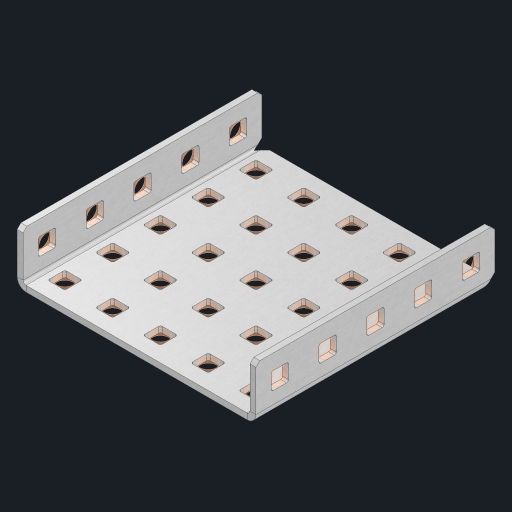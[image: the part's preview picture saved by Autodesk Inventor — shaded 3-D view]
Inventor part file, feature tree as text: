
AUTODESK INVENTOR PART (.ipt)
format: ipt  version: 2023 (Build 270158000, 158)  size: 696,320 bytes
history: native  units: in
note: dims shown in document units (in); Inventor stores cm internally (conversion verified against a paired STEP export)
features: other x40, extrude x34, sheet_metal_op x10, sketch x8, mirror x1, pattern_linear x1, chamfer x1
ambient origin geometry x8: Origin, YZ Plane, XZ Plane, XY Plane, X Axis, Y Axis, Z Axis, Center Point
bodies: Solid1 (feature_tree), Body (feature_tree)
feature tree (95):
  other  "Flange Pattern Plane"
  sheet_metal_op  "Flange Pattern"
  sheet_metal_op  "Body Pattern"
  other  "Arc Length"
  mirror  "Notch Mirror"
  pattern_linear  "Notch Pattern"  Spacing1=0.25in  [1 undecoded]
  chamfer  "End Chamfer"
  extrude  "Half Cut"  Depth=0.0625in
  sketch  "Sketch1"  dims[d0=2.5in]
  other  "Plate1"
  sketch  "Sketch2"  dims[d1=2.5in]
  other  "Plate2"
  sheet_metal_op  "Bend1"
  sheet_metal_op  "Corner1"
  sketch  "Sketch3"  dims[d2=0.0625in]
  other  "Flange Pattern Sketch"
  sketch  "Sketch7"  dims[d3=0.0625in]
  other  "Srf1"
  other  "Srf2"
  sketch  "Sketch8"  dims[d4=0.0312in]
  sketch  "Sketch9"  dims[d5=0.125in]
  other  "Srf91"
  sheet_metal_op  "Body Pattern Sketch"
  other  "Srf92"
  sketch  "Sketch13"  dims[d6=0.0625in]
  sketch  "Sketch14"  dims[d7=0.5in d8=90.0deg d9=0.0312in d10=0.25in d11=0.0625in d12=0.0625in d16=0.182in d17=0.02in d18=0.0625in d19=0.0in d20=0.25in d21=0.25in d46=0.172in d47=1.0in d48=0.0in d49=0.182in d50=0.02in d51=0.25in d52=0.25in d53=0.0625in d54=0.0in d55=0.172in d56=1.0in d57=0.0in d60=1.9685in d62=0.5in d63=1.9685in d65=0.5in d85=0.1473in d86=0.1782in d88=0.04in d89=0.0625in d90=0.0in d91=0.04in d92=0.0491in d95=2.5in d96=0.04in d97=0.25in d98=45.0deg d101=0.0in d102=2.497in d131=2.5in d132=1.9685in d134=0.5in d139=0.5in]
  other  "Srf856"
  other  "Srf1310"
  other  "Srf1311"
  other  "Srf1312"
  other  "Srf1376"
  other  "Srf1377"
  other  "Srf1728"
  other  "Srf1755"
  other  "Srf1878"
  other  "Srf1879"
  other  "Srf1880"
  other  "Srf1881"
  other  "Srf1942"
  other  "Srf1943"
  other  "Srf1944"
  other  "Srf1945"
  other  "Srf1946"
  other  "Srf1947"
  other  "Srf1948"
  other  "Srf1949"
  other  "Srf1950"
  other  "Srf1951"
  other  "Srf1952"
  other  "Srf1953"
  other  "Srf1954"
  other  "Srf1955"
  other  "Srf1956"
  other  "Srf1957"
  other  "Srf1958"
  other  "Srf1959"
  other  "Srf1960"
  sheet_metal_op  "Flange Stamp"
  sheet_metal_op  "Flange Circle"
  sheet_metal_op  "Body Stamp"
  sheet_metal_op  "Body Circle"
  sheet_metal_op  "Notch"
  extrude  "ExtrusionSrf2"  Depth=0.0625in
  extrude  "ExtrusionSrf92"  Depth=2.5in
  extrude  "ExtrusionSrf856"  Depth=0.02in
  extrude  "ExtrusionSrf1310"  Depth=0.0625in
  extrude  "ExtrusionSrf1311"  TaperAngle=0.0deg  [1 undecoded]
  extrude  "ExtrusionSrf1312"  Depth=0.25in
  extrude  "ExtrusionSrf1376"  Depth=0.25in
  extrude  "ExtrusionSrf1377"  Depth=2.5in
  extrude  "ExtrusionSrf1728"  Depth=2.5in TaperAngle=0.0deg
  extrude  "ExtrusionSrf1755"  Depth=2.5in
  extrude  "ExtrusionSrf1878"  Depth=0.02in
  extrude  "ExtrusionSrf1879"  Depth=0.25in
  extrude  "ExtrusionSrf1880"  Depth=0.25in
  extrude  "ExtrusionSrf1881"  Depth=0.0625in
  extrude  "ExtrusionSrf1942"  TaperAngle=0.0deg  [1 undecoded]
  extrude  "ExtrusionSrf1943"  Depth=2.5in
  extrude  "ExtrusionSrf1944"  Depth=2.5in TaperAngle=0.0deg
  extrude  "ExtrusionSrf1945"  Depth=2.5in
  extrude  "ExtrusionSrf1946"  Depth=2.5in
  extrude  "ExtrusionSrf1947"  Depth=2.5in
  extrude  "ExtrusionSrf1948"  Depth=2.5in
  extrude  "ExtrusionSrf1949"  Depth=2.5in
  extrude  "ExtrusionSrf1950"  Depth=0.0625in
  extrude  "ExtrusionSrf1951"  TaperAngle=0.0deg  [1 undecoded]
  extrude  "ExtrusionSrf1952"  Depth=2.5in
  extrude  "ExtrusionSrf1953"  Depth=2.5in
  extrude  "ExtrusionSrf1954"  Depth=2.5in
  extrude  "ExtrusionSrf1955"  Depth=0.25in TaperAngle=45.0deg
  extrude  "ExtrusionSrf1956"  TaperAngle=0.0deg  [1 undecoded]
  extrude  "ExtrusionSrf1957"  Depth=2.5in
  extrude  "ExtrusionSrf1958"  Depth=2.5in
  extrude  "ExtrusionSrf1959"  Depth=2.5in
  extrude  "ExtrusionSrf1960"  Depth=2.5in
note: 5 required parameter values undecoded (feature->parameter linkage not recoverable at this tier; creation-order binding heuristic only, values carry confidence <= 0.55)
